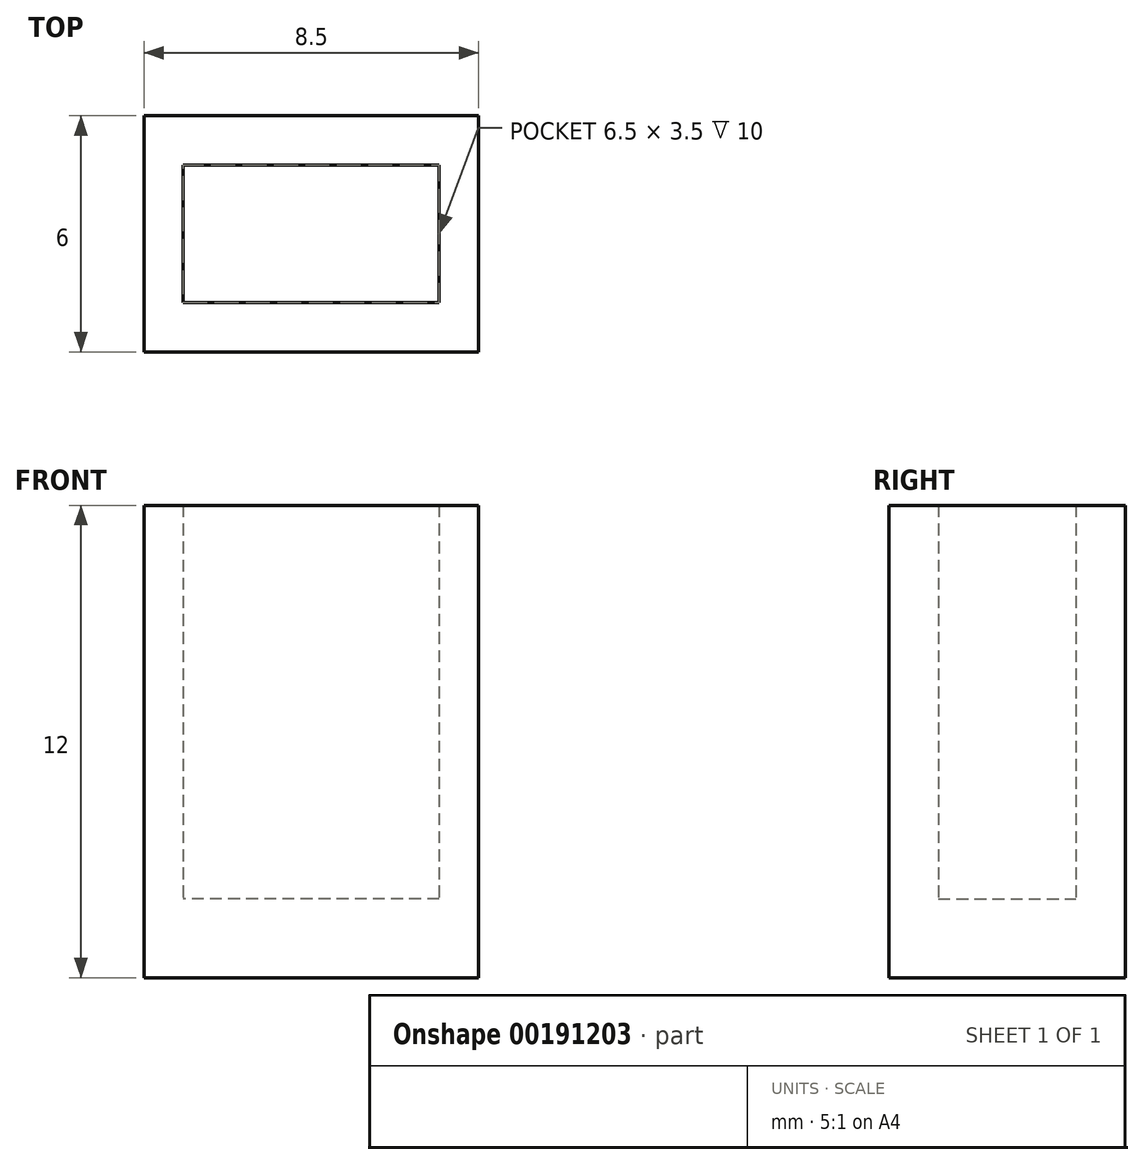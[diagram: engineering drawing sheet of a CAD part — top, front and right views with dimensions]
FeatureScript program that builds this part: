
annotation { "Feature Type Name" : "Feature", "Feature Type Description" : "" }
export const myFeature = defineFeature(function(context is Context, id is Id, definition is map)
    precondition{}
    {
        {
            var Q0;
            Q0=qCreatedBy(makeId("Top.planeOp"),FACE);
            var sketch = newSketch(context, id + "F0", { "sketchPlane" : qUnion([Q0])});
            skLineSegment(sketch, "E0.bottom", {"start": v(4.25, -3) * mm, "end": v(-4.25, -3) * mm});
            skLineSegment(sketch, "E0.top", {"start": v(4.25, 3) * mm, "end": v(-4.25, 3) * mm});
            skLineSegment(sketch, "E0.left", {"start": v(4.25, -3) * mm, "end": v(4.25, 3) * mm});
            skLineSegment(sketch, "E0.right", {"start": v(-4.25, -3) * mm, "end": v(-4.25, 3) * mm});
            skPoint(sketch, "E0.middle", {"position": v(0, 0) * mm});
            skSolve(sketch);
        }
        {
            var Q0;
            Q0 = qSketchRegion(id + "F0", true);
            extrude(context, id + "F1", {"entities" : qUnion([Q0]), "depth" : 2 * mm});
        }
        {
            var Q0;
            Q0=makeQuery(id+"F1.opExtrude","CAP_FACE",FACE,{"disambiguationData":[OSD([sQuery(id+"F0.wireOp",EDGE,"E0.bottom"),sQuery(id+"F0.wireOp",EDGE,"E0.top"),sQuery(id+"F0.wireOp",EDGE,"E0.left"),sQuery(id+"F0.wireOp",EDGE,"E0.right")])],"isStart":false});
            var sketch = newSketch(context, id + "F2", { "sketchPlane" : qUnion([Q0])});
            skLineSegment(sketch, "E1.bottom", {"start": v(4.25, -3) * mm, "end": v(-4.25, -3) * mm});
            skLineSegment(sketch, "E1.top", {"start": v(4.25, 3) * mm, "end": v(-4.25, 3) * mm});
            skLineSegment(sketch, "E1.left", {"start": v(4.25, -3) * mm, "end": v(4.25, 3) * mm});
            skLineSegment(sketch, "E1.right", {"start": v(-4.25, -3) * mm, "end": v(-4.25, 3) * mm});
            skPoint(sketch, "E1.middle", {"position": v(0, 0) * mm});
            skLineSegment(sketch, "E2.bottom", {"start": v(3.25, -1.75) * mm, "end": v(-3.25, -1.75) * mm});
            skLineSegment(sketch, "E2.top", {"start": v(3.25, 1.75) * mm, "end": v(-3.25, 1.75) * mm});
            skLineSegment(sketch, "E2.left", {"start": v(3.25, -1.75) * mm, "end": v(3.25, 1.75) * mm});
            skLineSegment(sketch, "E2.right", {"start": v(-3.25, -1.75) * mm, "end": v(-3.25, 1.75) * mm});
            skSolve(sketch);
        }
        {
            var Q0;
            Q0=makeQuery(id+"F2.imprint","IMPRINT",FACE,{"disambiguationData":[TD([[makeQuery(id+"F2.imprint","IMPRINT",EDGE,{"derivedFrom":sQuery(id+"F2.wireOp",EDGE,"E1.bottom")}),-1.0]])]});
            extrude(context, id + "F3", {"entities" : qUnion([Q0]), "operationType" : NewBodyOperationType.ADD, "depth" : 10 * mm});
        }
    });
